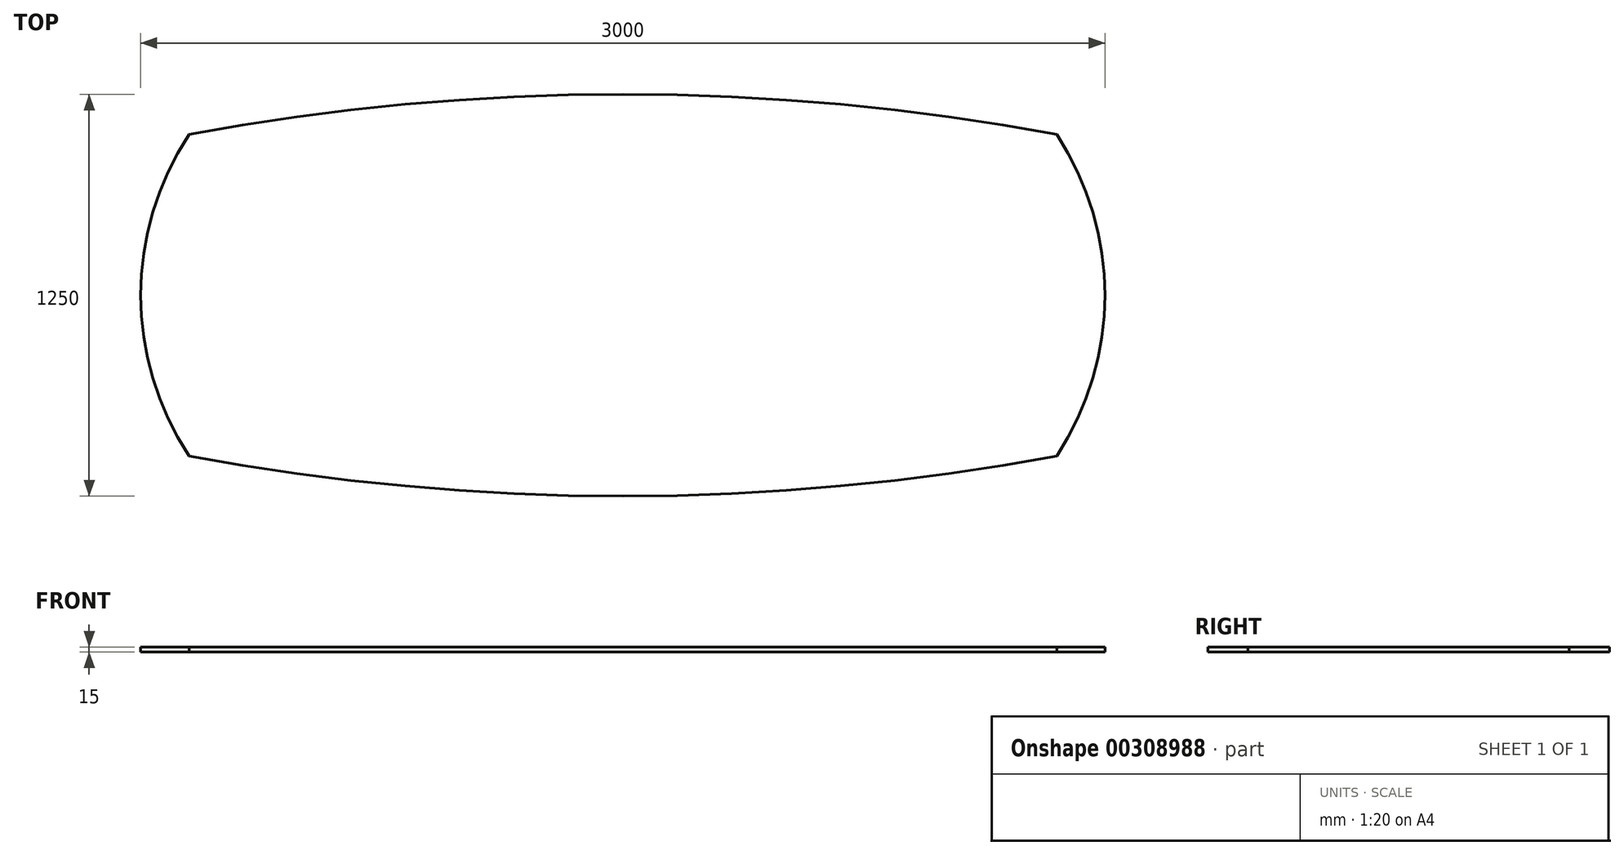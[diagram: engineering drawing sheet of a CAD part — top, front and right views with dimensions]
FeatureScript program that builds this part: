
annotation { "Feature Type Name" : "Feature", "Feature Type Description" : "" }
export const myFeature = defineFeature(function(context is Context, id is Id, definition is map)
    precondition{}
    {
        {
            var Q0;
            Q0=qCreatedBy(makeId("Top.planeOp"),FACE);
            cPlane(context, id + "F0", {"entities" : qUnion([Q0]), "cplaneType" : CPlaneType.OFFSET, "offset" : 1100 * mm, "width" : 150 * mm, "height" : 150 * mm});
        }
        {
            var Q0;
            Q0=qCreatedBy(id+"F0.planeOp",FACE);
            var sketch = newSketch(context, id + "F1", { "sketchPlane" : qUnion([Q0])});
            skLineSegment(sketch, "E0.bottom", {"start": v(-1500, 625) * mm, "end": v(1500, 625) * mm, "construction": true});
            skLineSegment(sketch, "E0.top", {"start": v(-1500, -625) * mm, "end": v(1500, -625) * mm, "construction": true});
            skLineSegment(sketch, "E0.left", {"start": v(-1500, 625) * mm, "end": v(-1500, -625) * mm, "construction": true});
            skLineSegment(sketch, "E0.right", {"start": v(1500, 625) * mm, "end": v(1500, -625) * mm, "construction": true});
            skPoint(sketch, "E1", {"position": v(-1500, 0) * mm});
            skPoint(sketch, "E2", {"position": v(0, 625) * mm});
            skArc(sketch, "E3", {"start": v(1350, 500) * mm, "mid": v(0, 625) * mm, "end": v(-1350, 500) * mm});
            skArc(sketch, "E4", {"start": v(-1350, -500) * mm, "mid": v(0, -625) * mm, "end": v(1350, -500) * mm});
            skArc(sketch, "E5", {"start": v(-1350, 500) * mm, "mid": v(-1500, 0) * mm, "end": v(-1350, -500) * mm});
            skArc(sketch, "E6", {"start": v(1350, -500) * mm, "mid": v(1500, 0) * mm, "end": v(1350, 500) * mm});
            skSolve(sketch);
        }
        {
            var Q0;
            Q0=makeQuery(id+"F1.imprint","IMPRINT",FACE,{"disambiguationData":[TD([[makeQuery(id+"F1.imprint","IMPRINT",EDGE,{"derivedFrom":sQuery(id+"F1.wireOp",EDGE,"E3")}),1.0]])]});
            extrude(context, id + "F2", {"entities" : qUnion([Q0]), "oppositeDirection" : true, "depth" : 15 * mm});
        }
        {
            var Q0;
            Q0=qCreatedBy(id+"F0.planeOp",FACE);
            cPlane(context, id + "F3", {"entities" : qUnion([Q0]), "cplaneType" : CPlaneType.OFFSET, "offset" : 40 * mm, "oppositeDirection" : true, "width" : 150 * mm, "height" : 150 * mm});
        }
    });
